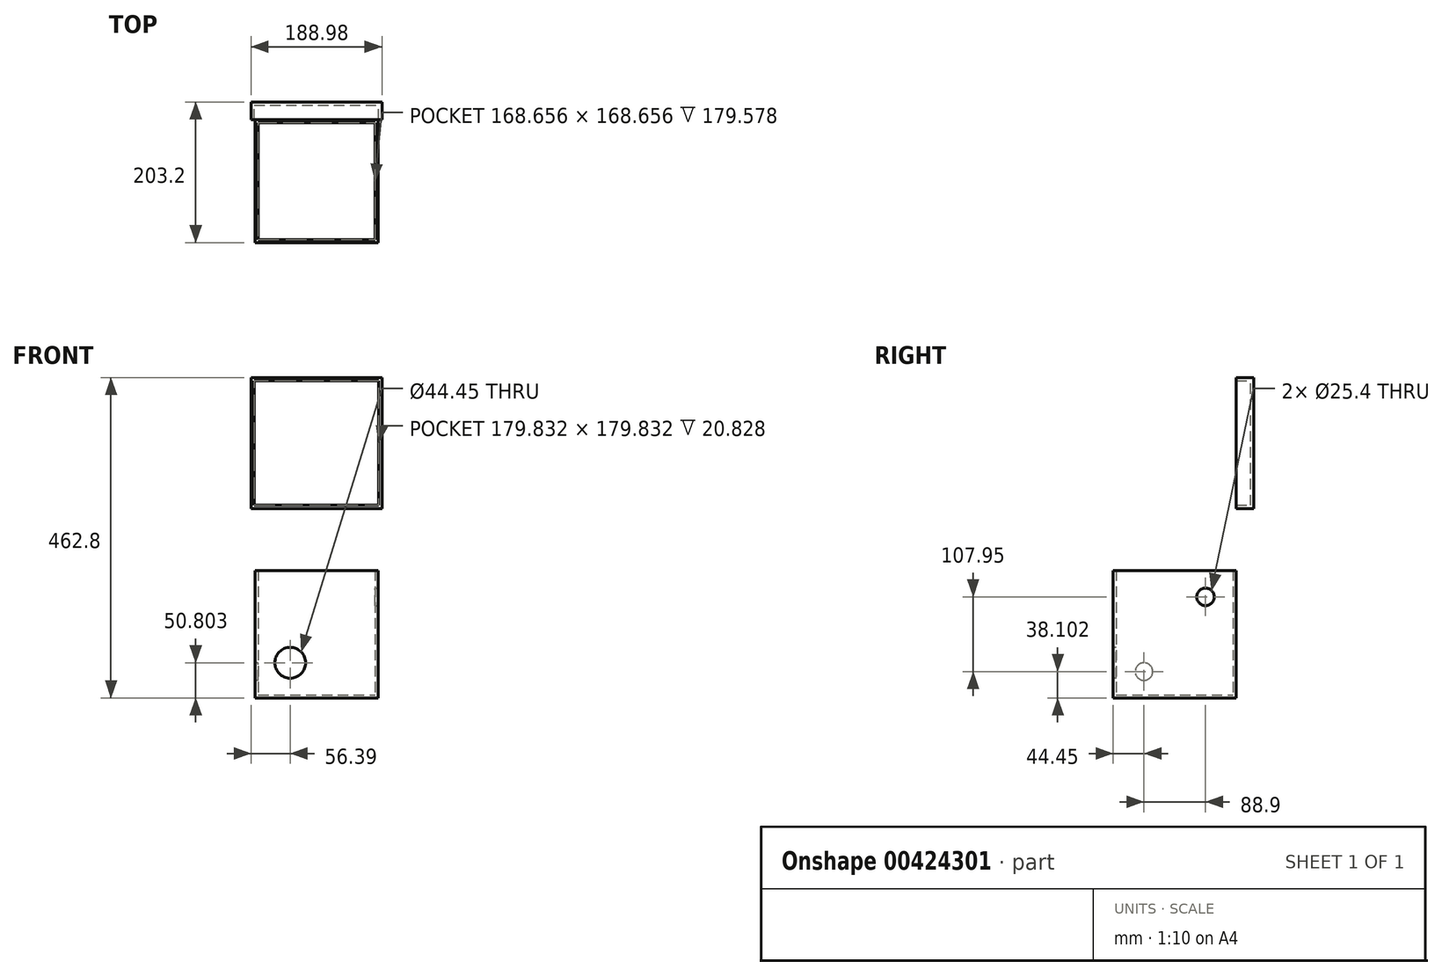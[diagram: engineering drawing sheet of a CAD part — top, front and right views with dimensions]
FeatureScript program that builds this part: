
annotation { "Feature Type Name" : "Feature", "Feature Type Description" : "" }
export const myFeature = defineFeature(function(context is Context, id is Id, definition is map)
    precondition{}
    {
        {
            var Q0;
            Q0=qCreatedBy(makeId("Front.planeOp"),FACE);
            var sketch = newSketch(context, id + "F0", { "sketchPlane" : qUnion([Q0])});
            skLineSegment(sketch, "E0.bottom", {"start": v(-75.6, 107.87) * mm, "end": v(102.2, 107.87) * mm});
            skLineSegment(sketch, "E0.top", {"start": v(-75.6, -76.28) * mm, "end": v(102.2, -76.28) * mm});
            skLineSegment(sketch, "E0.left", {"start": v(-75.6, 107.87) * mm, "end": v(-75.6, -76.28) * mm});
            skLineSegment(sketch, "E0.right", {"start": v(102.2, 107.87) * mm, "end": v(102.2, -76.28) * mm});
            skSolve(sketch);
        }
        {
            var Q0;
            Q0=makeQuery(id+"F0.imprint","IMPRINT",FACE,{"disambiguationData":[TD([[makeQuery(id+"F0.imprint","IMPRINT",EDGE,{"derivedFrom":sQuery(id+"F0.wireOp",EDGE,"E0.bottom")}),-1.0]])]});
            var Q1;
            Q1=sQuery(id+"F0.wireOp",EDGE,"E0.right");
            var Q2;
            Q2=sQuery(id+"F0.wireOp",EDGE,"E0.left");
            var Q3;
            Q3=sQuery(id+"F0.wireOp",EDGE,"E0.top");
            var Q4;
            Q4=sQuery(id+"F0.wireOp",EDGE,"E0.bottom");
            extrude(context, id + "F1", {"entities" : qUnion([Q0]), "surfaceEntities" : qUnion([Q1, Q2, Q3, Q4]), "depth" : 177.8 * mm});
        }
        {
            var Q0;
            Q0=makeQuery(id+"F1.opExtrude","SWEPT_FACE",FACE,{"disambiguationData":[OSD([sQuery(id+"F0.wireOp",EDGE,"E0.bottom")])]});
            shell(context, id + "F2", {"entities" : qUnion([Q0]), "thickness" : 4.57 * mm});
        }
        {
            var Q0;
            Q0=makeQuery(id+"F1.opExtrude","CAP_FACE",FACE,{"disambiguationData":[OSD([sQuery(id+"F0.wireOp",EDGE,"E0.bottom"),sQuery(id+"F0.wireOp",EDGE,"E0.top"),sQuery(id+"F0.wireOp",EDGE,"E0.left"),sQuery(id+"F0.wireOp",EDGE,"E0.right")])],"isStart":false});
            var sketch = newSketch(context, id + "F3", { "sketchPlane" : qUnion([Q0])});
            skLineSegment(sketch, "E1", {"start": v(13.3, 107.87) * mm, "end": v(13.3, -76.28) * mm, "construction": true});
            skLineSegment(sketch, "E2", {"start": v(13.3, -76.28) * mm, "end": v(-24.8, -76.28) * mm, "construction": true});
            skLineSegment(sketch, "E3", {"start": v(-75.6, -76.28) * mm, "end": v(-75.6, -25.48) * mm, "construction": true});
            skLineSegment(sketch, "E4", {"start": v(-75.6, -25.48) * mm, "end": v(13.3, -25.48) * mm, "construction": true});
            skLineSegment(sketch, "E5", {"start": v(-24.8, -76.28) * mm, "end": v(-24.8, -25.48) * mm, "construction": true});
            skCircle(sketch, "E6", {"center": v(-24.8, -25.48) * mm, "radius": 21.2 * mm, "construction": true});
            skSolve(sketch);
        }
        {
            var Q0;
            Q0=sQuery(id+"F3.wireOp",VERTEX,"E6.center");
            var Q1;
            Q1=makeQuery(id+"F1.opExtrude","SWEPT_BODY",BODY,{"disambiguationData":[OSD([sQuery(id+"F0.wireOp",EDGE,"E0.bottom"),sQuery(id+"F0.wireOp",EDGE,"E0.top"),sQuery(id+"F0.wireOp",EDGE,"E0.left"),sQuery(id+"F0.wireOp",EDGE,"E0.right")])]});
            hole(context, id + "F4", {"style" : HoleStyle.SIMPLE, "endStyle" : HoleEndStyle.BLIND, "holeDiameter" : 44.45 * mm, "holeDepth" : 12.7 * mm, "isTappedThrough" : true, "tappedDepth" : 12.7 * mm, "tapClearance" : 3, "locations" : qUnion([Q0]), "scope" : qUnion([Q1])});
        }
        {
            var Q0;
            Q0=makeQuery(id+"F1.opExtrude","SWEPT_FACE",FACE,{"disambiguationData":[OSD([sQuery(id+"F0.wireOp",EDGE,"E0.right")])]});
            var sketch = newSketch(context, id + "F5", { "sketchPlane" : qUnion([Q0])});
            skLineSegment(sketch, "E7", {"start": v(-88.9, 107.87) * mm, "end": v(-88.9, -76.28) * mm, "construction": true});
            skLineSegment(sketch, "E8", {"start": v(-88.9, 107.87) * mm, "end": v(-44.45, 107.87) * mm, "construction": true});
            skLineSegment(sketch, "E9", {"start": v(-88.9, 107.87) * mm, "end": v(-88.9, 69.77) * mm, "construction": true});
            skLineSegment(sketch, "E10", {"start": v(-88.9, 69.77) * mm, "end": v(-44.45, 69.77) * mm, "construction": true});
            skLineSegment(sketch, "E11", {"start": v(-44.45, 69.77) * mm, "end": v(-44.45, 107.87) * mm, "construction": true});
            skCircle(sketch, "E12", {"center": v(-44.45, 69.77) * mm, "radius": 11.94 * mm, "construction": true});
            skSolve(sketch);
        }
        {
            var Q0;
            Q0=sQuery(id+"F5.wireOp",VERTEX,"E10.end");
            var Q1;
            Q1=makeQuery(id+"F1.opExtrude","SWEPT_BODY",BODY,{"disambiguationData":[OSD([sQuery(id+"F0.wireOp",EDGE,"E0.bottom"),sQuery(id+"F0.wireOp",EDGE,"E0.top"),sQuery(id+"F0.wireOp",EDGE,"E0.left"),sQuery(id+"F0.wireOp",EDGE,"E0.right")])]});
            hole(context, id + "F6", {"style" : HoleStyle.SIMPLE, "endStyle" : HoleEndStyle.BLIND, "holeDiameter" : 25.4 * mm, "holeDepth" : 12.7 * mm, "isTappedThrough" : true, "tappedDepth" : 12.7 * mm, "tapClearance" : 3, "locations" : qUnion([Q0]), "scope" : qUnion([Q1])});
        }
        {
            var Q0;
            Q0=makeQuery(id+"F1.opExtrude","CAP_FACE",FACE,{"disambiguationData":[OSD([sQuery(id+"F0.wireOp",EDGE,"E0.bottom"),sQuery(id+"F0.wireOp",EDGE,"E0.top"),sQuery(id+"F0.wireOp",EDGE,"E0.left"),sQuery(id+"F0.wireOp",EDGE,"E0.right")])],"isStart":true});
            cPlane(context, id + "F7", {"entities" : qUnion([Q0]), "cplaneType" : CPlaneType.OFFSET, "offset" : 25.4 * mm, "width" : 152.4 * mm, "height" : 152.4 * mm});
        }
        {
            var Q0;
            Q0=qCreatedBy(id+"F7.planeOp",FACE);
            var sketch = newSketch(context, id + "F8", { "sketchPlane" : qUnion([Q0])});
            skLineSegment(sketch, "E13", {"start": v(-13.3, -254.74) * mm, "end": v(-13.3, 376.73) * mm, "construction": true});
            skPoint(sketch, "E13.startSnap0", {"position": v(-13.3, -76.28) * mm});
            skLineSegment(sketch, "E14.bottom", {"start": v(81.18, 197.55) * mm, "end": v(-107.8, 197.55) * mm});
            skLineSegment(sketch, "E14.top", {"start": v(81.18, 386.52) * mm, "end": v(-107.8, 386.52) * mm});
            skLineSegment(sketch, "E14.left", {"start": v(81.18, 197.55) * mm, "end": v(81.18, 386.52) * mm});
            skLineSegment(sketch, "E14.right", {"start": v(-107.8, 197.55) * mm, "end": v(-107.8, 386.52) * mm});
            skPoint(sketch, "E14.middle", {"position": v(-13.3, 292.04) * mm});
            skSolve(sketch);
        }
        {
            var Q0;
            Q0=makeQuery(id+"F8.imprint","IMPRINT",FACE,{"disambiguationData":[TD([[makeQuery(id+"F8.imprint","IMPRINT",EDGE,{"derivedFrom":sQuery(id+"F8.wireOp",EDGE,"E14.bottom")}),-1.0]])]});
            extrude(context, id + "F9", {"entities" : qUnion([Q0]), "oppositeDirection" : true, "depth" : 25.4 * mm});
        }
        {
            var Q0;
            Q0=makeQuery(id+"F9.opExtrude","CAP_FACE",FACE,{"disambiguationData":[OSD([sQuery(id+"F8.wireOp",EDGE,"E14.bottom"),sQuery(id+"F8.wireOp",EDGE,"E14.top"),sQuery(id+"F8.wireOp",EDGE,"E14.left"),sQuery(id+"F8.wireOp",EDGE,"E14.right")])],"isStart":false});
            shell(context, id + "F10", {"entities" : qUnion([Q0]), "thickness" : 4.57 * mm});
        }
        {
            var Q0;
            Q0=makeQuery(id+"F1.opExtrude","SWEPT_FACE",FACE,{"disambiguationData":[OSD([sQuery(id+"F0.wireOp",EDGE,"E0.left")])]});
            var sketch = newSketch(context, id + "F11", { "sketchPlane" : qUnion([Q0])});
            skLineSegment(sketch, "E15", {"start": v(88.9, -76.28) * mm, "end": v(88.9, 107.87) * mm, "construction": true});
            skLineSegment(sketch, "E16", {"start": v(88.9, -76.28) * mm, "end": v(88.9, -38.18) * mm});
            skLineSegment(sketch, "E17", {"start": v(88.9, -38.18) * mm, "end": v(133.35, -38.18) * mm, "construction": true});
            skLineSegment(sketch, "E18", {"start": v(133.35, -38.18) * mm, "end": v(133.35, -76.28) * mm, "construction": true});
            skCircle(sketch, "E19", {"center": v(133.35, -38.18) * mm, "radius": 11.94 * mm, "construction": true});
            skSolve(sketch);
        }
        {
            var Q0;
            Q0=sQuery(id+"F11.wireOp",VERTEX,"E19.center");
            var Q1;
            Q1=makeQuery(id+"F1.opExtrude","SWEPT_BODY",BODY,{"disambiguationData":[OSD([sQuery(id+"F0.wireOp",EDGE,"E0.bottom"),sQuery(id+"F0.wireOp",EDGE,"E0.top"),sQuery(id+"F0.wireOp",EDGE,"E0.left"),sQuery(id+"F0.wireOp",EDGE,"E0.right")])]});
            hole(context, id + "F12", {"style" : HoleStyle.SIMPLE, "endStyle" : HoleEndStyle.BLIND, "holeDiameter" : 25.4 * mm, "holeDepth" : 12.7 * mm, "isTappedThrough" : true, "tappedDepth" : 12.7 * mm, "tapClearance" : 3, "locations" : qUnion([Q0]), "scope" : qUnion([Q1])});
        }
    });
